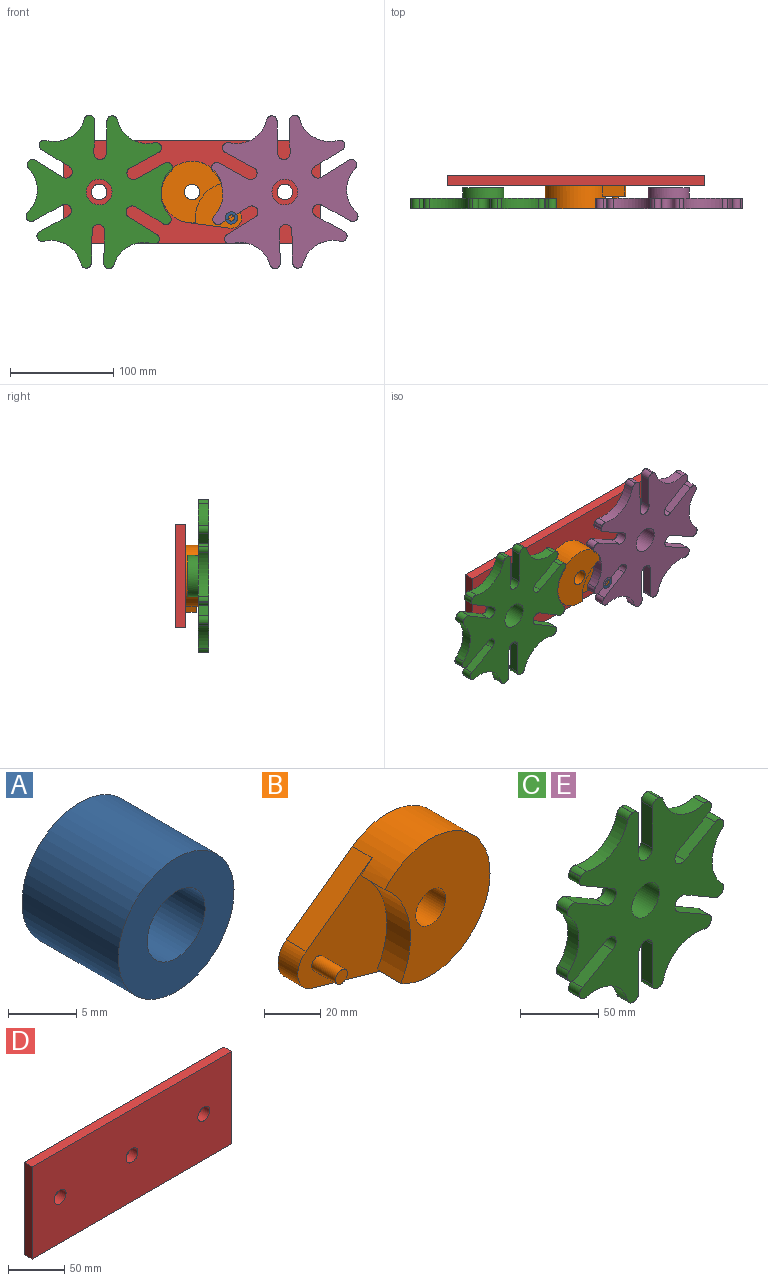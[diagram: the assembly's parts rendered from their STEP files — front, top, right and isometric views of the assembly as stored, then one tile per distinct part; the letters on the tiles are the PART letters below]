
ASSEMBLY  parts=5 mates=4
PART A: 4 faces, bbox 12x10x12 mm
  f0: cylinder r=3mm len=10mm, axis (0,1,0), area 188.5mm2, adj f2,f3
  f1: cylinder r=6mm len=12mm, axis (0,1,0), area 377mm2, adj f2,f3
  f2: plane 12x12mm, normal (0,-1,0), area 84.8mm2, adj f0,f1
  f3: plane 12x12mm, normal (0,1,0), area 84.8mm2, adj f0,f1
PART B: 11 faces, bbox 84.9x22x59.8 mm
  f0: cylinder r=7.5mm len=22mm, axis (0,1,0), area 1036.7mm2, adj f2,f8
  f1: cylinder r=29.9mm len=59.8mm, axis (0,1,0), area 2840.8mm2, adj f2,f5,f6,f8,f9,f10
  f2: plane 59.8x52.91mm, normal (0,-1,0), area 2032.2mm2, adj f0,f1,f10
  f3: cylinder r=3mm len=12mm, axis (0,1,0), area 226.2mm2, adj f4,f9
  f4: plane 6x6mm, normal (0,-1,0), area 28.3mm2, adj f3
  f5: plane 33.35x24.08mm, normal (-0.59,0,0.81), area 411.3mm2, adj f1,f7,f8,f9
  f6: plane 39.58x11.21mm, normal (-0.27,0,-0.96), area 411.3mm2, adj f1,f7,f8,f9
  f7: cylinder r=10mm len=17.73mm, axis (0,-1,0), area 224mm2, adj f5,f6,f8,f9
  f8: plane 84.9x59.8mm, normal (0,1,0), area 3383.7mm2, adj f0,f1,f5,f6,f7
  f9: plane 53.01x46.86mm, normal (0,-1,0), area 1323.3mm2, adj f1,f3,f5,f6,f7,f10
  f10: cylinder r=34.85mm len=44.91mm, axis (0,-1,0), area 596.6mm2, adj f1,f2,f9
PART C: 65 faces, bbox 140.8x20x148.3 mm
  f0: cylinder r=75mm len=10mm, axis (0,1,0), area 1.4mm2, adj f37,f38,f39,f62
  f1: plane 31.61x10mm, normal (1,0,0), area 316.1mm2, adj f2,f37,f38,f39
  f2: cylinder r=6mm len=12mm, axis (0,1,0), area 188.5mm2, adj f1,f3,f37,f38
  f3: plane 31.61x10mm, normal (-1,0,0), area 316.1mm2, adj f2,f37,f38,f40
  f4: cylinder r=75mm len=10mm, axis (0,1,0), area 1.4mm2, adj f37,f38,f40,f41
  f5: cylinder r=30mm len=36.99mm, axis (0,1,0), area 475.2mm2, adj f37,f38,f41,f42
  f6: cylinder r=75mm len=10mm, axis (0,1,0), area 1.4mm2, adj f37,f38,f42,f43
  f7: plane 27.37x15.8mm, normal (0.5,0,0.87), area 316.1mm2, adj f8,f37,f38,f43
  f8: cylinder r=6mm len=11.2mm, axis (0,1,0), area 188.5mm2, adj f7,f9,f37,f38
  f9: plane 27.37x15.8mm, normal (-0.5,0,-0.87), area 316.1mm2, adj f8,f37,f38,f44
  f10: cylinder r=75mm len=10mm, axis (0,1,0), area 1.4mm2, adj f37,f38,f44,f45
  f11: cylinder r=30mm len=42.71mm, axis (0,1,0), area 475.2mm2, adj f37,f38,f45,f46
  f12: cylinder r=75mm len=10mm, axis (0,1,0), area 1.4mm2, adj f37,f38,f46,f47
  f13: plane 27.37x15.8mm, normal (-0.5,0,0.87), area 316.1mm2, adj f14,f37,f38,f47
  f14: cylinder r=6mm len=11.2mm, axis (0,1,0), area 188.5mm2, adj f13,f15,f37,f38
  f15: plane 27.37x15.8mm, normal (0.5,0,-0.87), area 316.1mm2, adj f14,f37,f38,f48
  f16: cylinder r=75mm len=10mm, axis (0,1,0), area 1.4mm2, adj f37,f38,f48,f49
  f17: cylinder r=30mm len=36.99mm, axis (0,1,0), area 475.2mm2, adj f37,f38,f49,f50
  f18: cylinder r=75mm len=10mm, axis (0,1,0), area 1.4mm2, adj f37,f38,f50,f51
  f19: plane 31.61x10mm, normal (-1,0,0), area 316.1mm2, adj f20,f37,f38,f51
  f20: cylinder r=6mm len=12mm, axis (0,1,0), area 188.5mm2, adj f19,f21,f37,f38
  f21: plane 31.61x10mm, normal (1,0,0), area 316.1mm2, adj f20,f37,f38,f52
  f22: cylinder r=75mm len=10mm, axis (0,1,0), area 1.4mm2, adj f37,f38,f52,f53
  f23: cylinder r=30mm len=36.99mm, axis (0,1,0), area 475.2mm2, adj f37,f38,f53,f54
  f24: cylinder r=75mm len=10mm, axis (0,1,0), area 1.4mm2, adj f37,f38,f54,f55
  f25: plane 27.37x15.8mm, normal (-0.5,0,-0.87), area 316.1mm2, adj f26,f37,f38,f55
  f26: cylinder r=6mm len=11.2mm, axis (0,1,0), area 188.5mm2, adj f25,f27,f37,f38
  f27: plane 27.37x15.8mm, normal (0.5,0,0.87), area 316.1mm2, adj f26,f37,f38,f56
  f28: cylinder r=75mm len=10mm, axis (0,1,0), area 1.4mm2, adj f37,f38,f56,f57
  f29: cylinder r=30mm len=42.71mm, axis (0,1,0), area 475.2mm2, adj f37,f38,f57,f58
  f30: cylinder r=75mm len=10mm, axis (0,1,0), area 1.4mm2, adj f37,f38,f58,f59
  f31: plane 27.37x15.8mm, normal (0.5,0,-0.87), area 316.1mm2, adj f32,f37,f38,f59
  f32: cylinder r=6mm len=11.2mm, axis (0,1,0), area 188.5mm2, adj f31,f33,f37,f38
  f33: plane 27.37x15.8mm, normal (-0.5,0,0.87), area 316.1mm2, adj f32,f37,f38,f60
  f34: cylinder r=75mm len=10mm, axis (0,1,0), area 1.4mm2, adj f37,f38,f60,f61
  f35: cylinder r=12.5mm len=25mm, axis (0,1,0), area 1570.8mm2, adj f37,f64
  f36: cylinder r=30mm len=36.99mm, axis (0,1,0), area 475.2mm2, adj f37,f38,f61,f62
  f37: plane 148.26x140.83mm, normal (0,-1,0), area 11130.3mm2, adj f0,f1,f2,f3,f4,f5,f6,f7
  f38: plane 148.26x140.83mm, normal (0,1,0), area 10364.5mm2, adj f0,f1,f2,f3,f4,f5,f6,f7
  f39: cylinder r=5mm len=10mm, axis (0,1,0), area 86.4mm2, adj f0,f1,f37,f38
  f40: cylinder r=5mm len=10mm, axis (0,1,0), area 86.4mm2, adj f3,f4,f37,f38
  f41: cylinder r=5mm len=10mm, axis (0,-1,0), area 57.8mm2, adj f4,f5,f37,f38
  f42: cylinder r=5mm len=10mm, axis (0,-1,0), area 57.8mm2, adj f5,f6,f37,f38
  f43: cylinder r=5mm len=10mm, axis (0,1,0), area 86.4mm2, adj f6,f7,f37,f38
  f44: cylinder r=5mm len=10mm, axis (0,1,0), area 86.4mm2, adj f9,f10,f37,f38
  f45: cylinder r=5mm len=10mm, axis (0,-1,0), area 57.8mm2, adj f10,f11,f37,f38
  f46: cylinder r=5mm len=10mm, axis (0,-1,0), area 57.8mm2, adj f11,f12,f37,f38
  f47: cylinder r=5mm len=10mm, axis (0,1,0), area 86.4mm2, adj f12,f13,f37,f38
  f48: cylinder r=5mm len=10mm, axis (0,1,0), area 86.4mm2, adj f15,f16,f37,f38
  f49: cylinder r=5mm len=10mm, axis (0,-1,0), area 57.8mm2, adj f16,f17,f37,f38
  f50: cylinder r=5mm len=10mm, axis (0,-1,0), area 57.8mm2, adj f17,f18,f37,f38
  f51: cylinder r=5mm len=10mm, axis (0,1,0), area 86.4mm2, adj f18,f19,f37,f38
  f52: cylinder r=5mm len=10mm, axis (0,1,0), area 86.4mm2, adj f21,f22,f37,f38
  f53: cylinder r=5mm len=10mm, axis (0,-1,0), area 57.8mm2, adj f22,f23,f37,f38
  f54: cylinder r=5mm len=10mm, axis (0,-1,0), area 57.8mm2, adj f23,f24,f37,f38
  f55: cylinder r=5mm len=10mm, axis (0,1,0), area 86.4mm2, adj f24,f25,f37,f38
  f56: cylinder r=5mm len=10mm, axis (0,1,0), area 86.4mm2, adj f27,f28,f37,f38
  f57: cylinder r=5mm len=10mm, axis (0,-1,0), area 57.8mm2, adj f28,f29,f37,f38
  f58: cylinder r=5mm len=10mm, axis (0,-1,0), area 57.8mm2, adj f29,f30,f37,f38
  f59: cylinder r=5mm len=10mm, axis (0,1,0), area 86.4mm2, adj f30,f31,f37,f38
  f60: cylinder r=5mm len=10mm, axis (0,1,0), area 86.4mm2, adj f33,f34,f37,f38
  f61: cylinder r=5mm len=10mm, axis (0,-1,0), area 57.8mm2, adj f34,f36,f37,f38
  f62: cylinder r=5mm len=10mm, axis (0,-1,0), area 57.8mm2, adj f0,f36,f37,f38
  f63: cylinder r=20mm len=40mm, axis (0,-1,0), area 1256.6mm2, adj f38,f64
  f64: plane 40x40mm, normal (0,1,0), area 765.8mm2, adj f35,f63
PART D: 9 faces, bbox 250x10x100 mm
  f0: plane 100x10mm, normal (-1,0,0), area 1000mm2, adj f1,f5,f7,f8
  f1: plane 250x10mm, normal (0,0,-1), area 2500mm2, adj f0,f2,f7,f8
  f2: plane 100x10mm, normal (1,0,0), area 1000mm2, adj f1,f5,f7,f8
  f3: cylinder r=7.5mm len=15mm, axis (0,1,0), area 471.2mm2, adj f7,f8
  f4: cylinder r=7.5mm len=15mm, axis (0,1,0), area 471.2mm2, adj f7,f8
  f5: plane 250x10mm, normal (0,0,1), area 2500mm2, adj f0,f2,f7,f8
  f6: cylinder r=7.5mm len=15mm, axis (0,1,0), area 471.2mm2, adj f7,f8
  f7: plane 250x100mm, normal (0,-1,0), area 24469.9mm2, adj f0,f1,f2,f3,f4,f5,f6
  f8: plane 250x100mm, normal (0,1,0), area 24469.9mm2, adj f0,f1,f2,f3,f4,f5,f6
PART E: same geometry as C
PLACE A rot(axis=(0,-1,0),104.5deg) t=(121.89,28.25,7.9)mm
PLACE B rot(axis=(0,-1,0),136.6deg) t=(102.23,8.25,41.25)mm
PLACE C rot(axis=(0,-1,0),118.7deg) t=(-74.03,8.25,15.58)mm
PLACE D t=(15.97,30.25,15.58)mm fixed
PLACE E rot(axis=(0,1,0),118.7deg) t=(105.97,8.25,15.58)mm
MATE revolute C.f35 <-> D.f4  axis (0,1,0) through (-74.03,18.25,15.58)mm
MATE revolute A.f0 <-> B.f3  axis (0,1,0) through (54.11,-1.75,-9.59)mm
MATE revolute E.f35 <-> D.f3  axis (0,1,0) through (105.97,18.25,15.58)mm
MATE revolute B.f0 <-> D.f6  axis (0,1,0) through (15.97,20.25,15.58)mm
